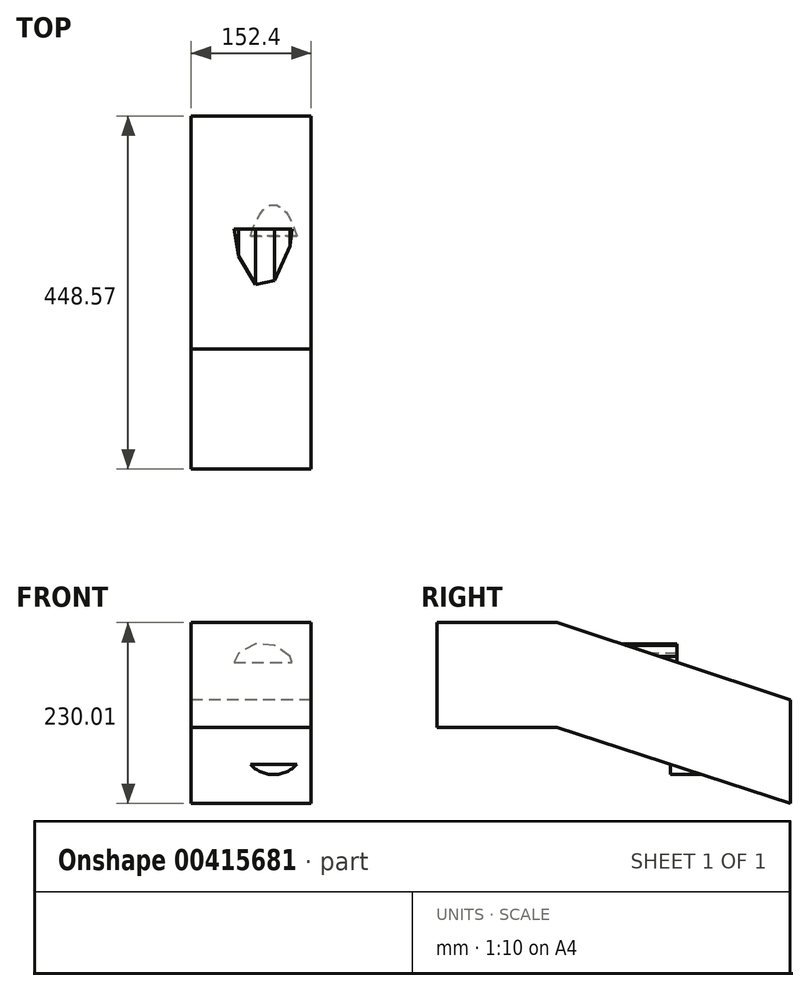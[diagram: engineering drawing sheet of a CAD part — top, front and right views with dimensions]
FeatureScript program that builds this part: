
annotation { "Feature Type Name" : "Feature", "Feature Type Description" : "" }
export const myFeature = defineFeature(function(context is Context, id is Id, definition is map)
    precondition{}
    {
        {
            var Q0;
            Q0=qCreatedBy(makeId("Right.planeOp"),FACE);
            var sketch = newSketch(context, id + "F0", { "sketchPlane" : qUnion([Q0])});
            skLineSegment(sketch, "E0", {"start": v(133.2, 35.03) * mm, "end": v(133.2, -96.87) * mm});
            skLineSegment(sketch, "E1", {"start": v(133.2, -96.87) * mm, "end": v(-162.97, 0) * mm});
            skLineSegment(sketch, "E2", {"start": v(-162.97, 0) * mm, "end": v(-162.97, 133.14) * mm});
            skLineSegment(sketch, "E3", {"start": v(-162.97, 133.14) * mm, "end": v(133.2, 35.03) * mm});
            skSolve(sketch);
        }
        {
            var Q0;
            Q0 = qSketchRegion(id + "F0", true);
            extrude(context, id + "F1", {"entities" : qUnion([Q0]), "depth" : 152.4 * mm});
        }
        {
            var Q0;
            Q0=makeQuery(id+"F1.opExtrude","SWEPT_FACE",FACE,{"disambiguationData":[OSD([sQuery(id+"F0.wireOp",EDGE,"E0")])]});
            var sketch = newSketch(context, id + "F2", { "sketchPlane" : qUnion([Q0])});
            skCircle(sketch, "E4", {"center": v(-104.68, -19.83) * mm, "radius": 40.18 * mm});
            skSolve(sketch);
        }
        {
            var Q0;
            Q0=makeQuery(id+"F2.imprint","IMPRINT",FACE,{"disambiguationData":[TD([[makeQuery(id+"F2.imprint","IMPRINT",EDGE,{"derivedFrom":sQuery(id+"F2.wireOp",EDGE,"E4")}),1.0]])]});
            extrude(context, id + "F3", {"entities" : qUnion([Q0]), "operationType" : NewBodyOperationType.ADD, "oppositeDirection" : true, "depth" : 152.4 * mm});
        }
        {
            var Q0;
            Q0=makeQuery(id+"F1.opExtrude","SWEPT_FACE",FACE,{"disambiguationData":[OSD([sQuery(id+"F0.wireOp",EDGE,"E2")])]});
            var sketch = newSketch(context, id + "F4", { "sketchPlane" : qUnion([Q0])});
            skSolve(sketch);
        }
        {
            var Q0;
            {var subQ0=sQuery(id+"F0.wireOp",EDGE,"E2");Q0=makeQuery(id+"F4.imprint","IMPRINT",FACE,{"disambiguationData":[TD([[makeQuery(id+"F4.imprint","IMPRINT",EDGE,{"derivedFrom":makeQuery(id+"F1.opExtrude","CAP_EDGE",EDGE,{"disambiguationData":[OSD([subQ0])],"isStart":true})}),-1.0]])]});}
            var sketch = newSketch(context, id + "F5", { "sketchPlane" : qUnion([Q0])});
            skCircle(sketch, "E5.cCircle", {"center": v(91.16, 63.63) * mm, "radius": 41.55 * mm, "construction": true});
            skLineSegment(sketch, "E5.0", {"start": v(65.4, 28.8) * mm, "end": v(50.67, 48.26) * mm});
            skLineSegment(sketch, "E5.1", {"start": v(50.67, 48.26) * mm, "end": v(48.8, 72.6) * mm});
            skLineSegment(sketch, "E5.2", {"start": v(48.8, 72.6) * mm, "end": v(60.36, 94.08) * mm});
            skLineSegment(sketch, "E5.3", {"start": v(60.36, 94.08) * mm, "end": v(81.71, 105.9) * mm});
            skLineSegment(sketch, "E5.4", {"start": v(81.71, 105.9) * mm, "end": v(106.07, 104.3) * mm});
            skLineSegment(sketch, "E5.5", {"start": v(106.07, 104.3) * mm, "end": v(125.68, 89.78) * mm});
            skLineSegment(sketch, "E5.6", {"start": v(125.68, 89.78) * mm, "end": v(134.34, 66.96) * mm});
            skLineSegment(sketch, "E5.7", {"start": v(134.34, 66.96) * mm, "end": v(129.3, 43.09) * mm});
            skLineSegment(sketch, "E5.8", {"start": v(129.3, 43.09) * mm, "end": v(112.14, 25.74) * mm});
            skLineSegment(sketch, "E5.9", {"start": v(112.14, 25.74) * mm, "end": v(88.32, 20.41) * mm});
            skLineSegment(sketch, "E5.10", {"start": v(88.32, 20.41) * mm, "end": v(65.4, 28.8) * mm});
            skPoint(sketch, "E5.0.midPoint", {"position": v(58.04, 38.53) * mm});
            skSolve(sketch);
        }
        {
            var Q0;
            Q0 = qSketchRegion(id + "F5", true);
            extrude(context, id + "F6", {"entities" : qUnion([Q0]), "operationType" : NewBodyOperationType.ADD, "oppositeDirection" : true, "depth" : 152.4 * mm});
        }
        {
            var Q0;
            {var subQ0=sQuery(id+"F0.wireOp",EDGE,"E2");Q0=makeQuery(id+"F4.imprint","IMPRINT",FACE,{"disambiguationData":[TD([[makeQuery(id+"F4.imprint","IMPRINT",EDGE,{"derivedFrom":makeQuery(id+"F1.opExtrude","CAP_EDGE",EDGE,{"disambiguationData":[OSD([subQ0])],"isStart":true})}),-1.0]])]});}
            extrude(context, id + "F7", {"entities" : qUnion([Q0]), "operationType" : NewBodyOperationType.ADD, "depth" : 152.4 * mm});
        }
    });
